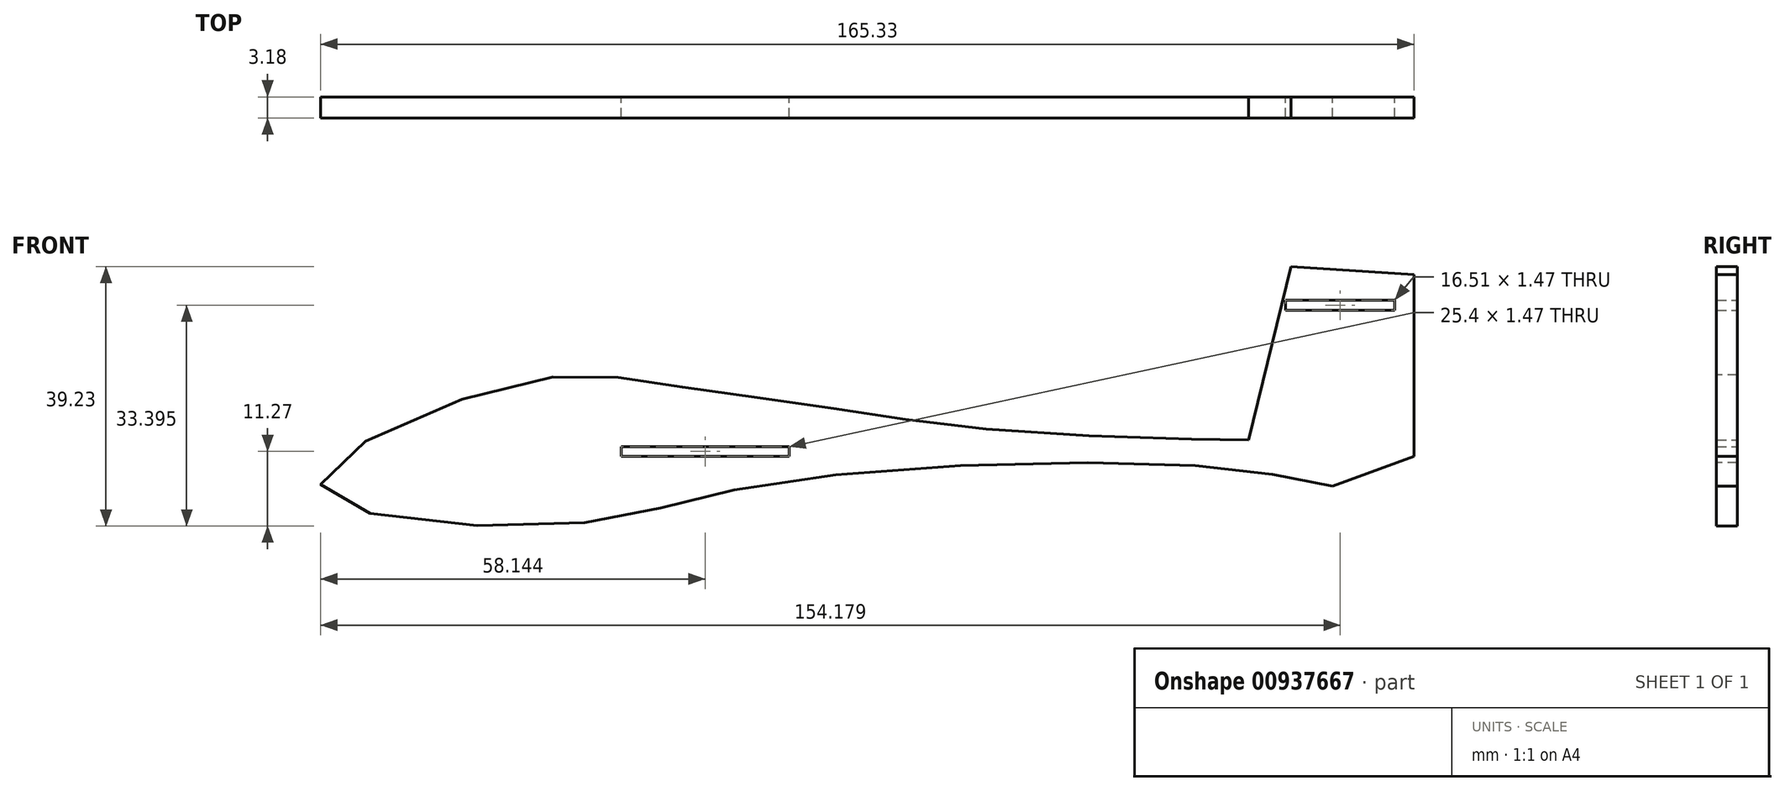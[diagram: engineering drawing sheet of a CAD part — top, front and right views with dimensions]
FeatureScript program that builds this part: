
annotation { "Feature Type Name" : "Feature", "Feature Type Description" : "" }
export const myFeature = defineFeature(function(context is Context, id is Id, definition is map)
    precondition{}
    {
        {
            var Q0;
            Q0=qCreatedBy(makeId("Front.planeOp"),FACE);
            var sketch = newSketch(context, id + "F0", { "sketchPlane" : qUnion([Q0])});
            skLineSegment(sketch, "E0.bottom", {"start": v(-114.3, 50.8) * mm, "end": v(114.3, 50.8) * mm, "construction": true});
            skLineSegment(sketch, "E0.top", {"start": v(-114.3, -50.8) * mm, "end": v(114.3, -50.8) * mm, "construction": true});
            skLineSegment(sketch, "E0.left", {"start": v(-114.3, 50.8) * mm, "end": v(-114.3, -50.8) * mm, "construction": true});
            skLineSegment(sketch, "E0.right", {"start": v(114.3, 50.8) * mm, "end": v(114.3, -50.8) * mm, "construction": true});
            skPoint(sketch, "E0.middle", {"position": v(0, 0) * mm});
            skLineSegment(sketch, "E1", {"start": v(75.99, 16.43) * mm, "end": v(75.99, -11.05) * mm});
            skLineSegment(sketch, "E2", {"start": v(75.99, -11.05) * mm, "end": v(63.68, -15.56) * mm});
            skFitSpline(sketch, "E3", {"points": [v(63.68, -15.56) * mm, v(40.3, -12.28) * mm, v(-24.1, -15.56) * mm, v(-52.4, -21.3) * mm, v(-89.31, -15.56) * mm, v(-59.78, 0) * mm, v(-38.45, 0) * mm, v(-12.61, -3.67) * mm, v(16.51, -7.36) * mm, v(50.96, -8.59) * mm, v(51.37, -8.59) * mm], "startDerivative": vector(-201.77, 43.34) * mm, "endDerivative": vector(17.54, 0.24) * mm});
            skLineSegment(sketch, "E4", {"start": v(50.96, -8.59) * mm, "end": v(57.37, 17.66) * mm});
            skLineSegment(sketch, "E5", {"start": v(57.37, 17.66) * mm, "end": v(75.99, 16.43) * mm});
            skLineSegment(sketch, "E6.bottom", {"start": v(-43.9, -11.04) * mm, "end": v(-18.5, -11.04) * mm});
            skLineSegment(sketch, "E6.top", {"start": v(-43.9, -9.56) * mm, "end": v(-18.5, -9.56) * mm});
            skLineSegment(sketch, "E6.left", {"start": v(-43.9, -11.04) * mm, "end": v(-43.9, -9.56) * mm});
            skLineSegment(sketch, "E6.right", {"start": v(-18.5, -11.04) * mm, "end": v(-18.5, -9.56) * mm});
            skPoint(sketch, "E6.middle", {"position": v(-31.2, -10.3) * mm});
            skLineSegment(sketch, "E7.bottom", {"start": v(73.1, 11.09) * mm, "end": v(56.58, 11.09) * mm});
            skLineSegment(sketch, "E7.top", {"start": v(73.1, 12.56) * mm, "end": v(56.58, 12.56) * mm});
            skLineSegment(sketch, "E7.left", {"start": v(73.1, 11.09) * mm, "end": v(73.1, 12.56) * mm});
            skLineSegment(sketch, "E7.right", {"start": v(56.58, 11.09) * mm, "end": v(56.58, 12.56) * mm});
            skPoint(sketch, "E7.middle", {"position": v(64.84, 11.83) * mm});
            skSolve(sketch);
        }
        {
            var Q0;
            Q0 = qSketchRegion(id + "F0", true);
            extrude(context, id + "F1", {"entities" : qUnion([Q0]), "endBound" : BoundingType.SYMMETRIC, "depth" : 3.17 * mm, "offsetDistance" : 25.4 * mm});
        }
    });
